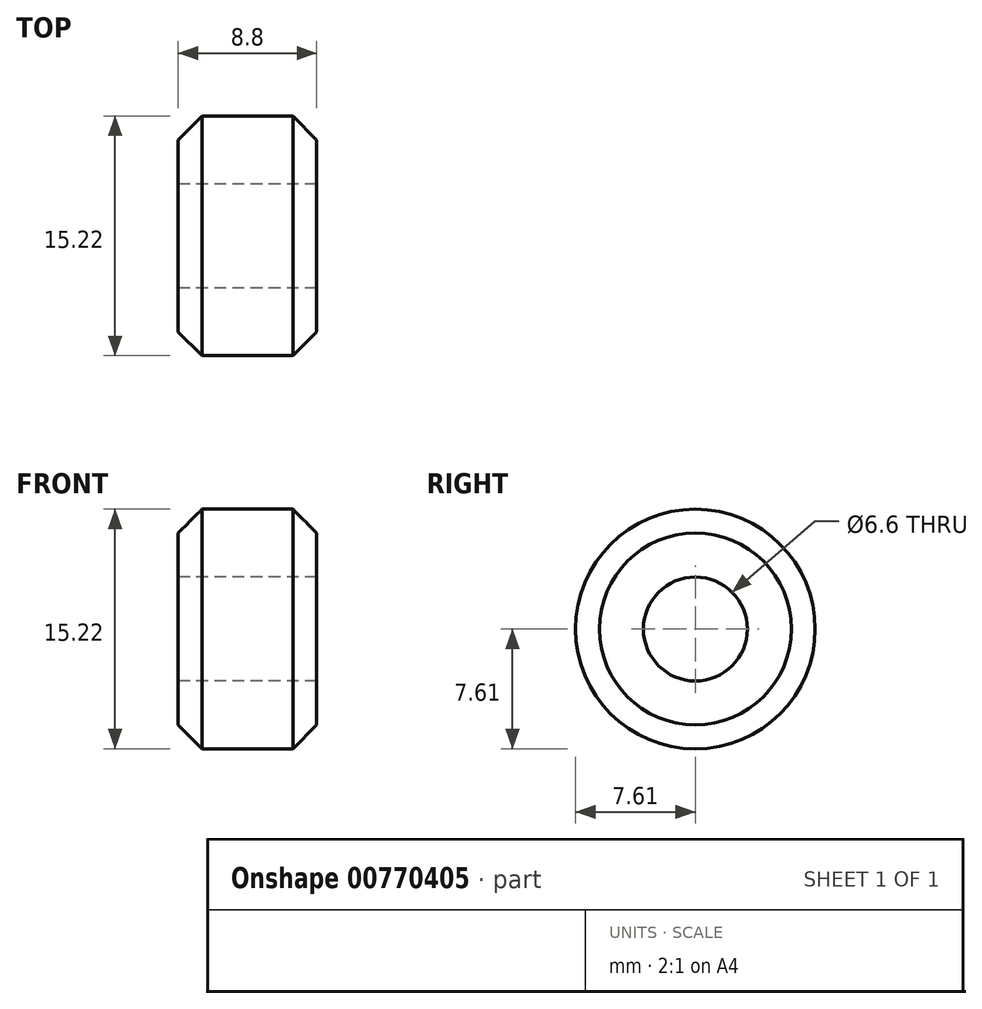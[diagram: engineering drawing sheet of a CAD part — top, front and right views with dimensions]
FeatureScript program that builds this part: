
annotation { "Feature Type Name" : "Feature", "Feature Type Description" : "" }
export const myFeature = defineFeature(function(context is Context, id is Id, definition is map)
    precondition{}
    {
        {
            var Q0;
            Q0=qCreatedBy(makeId("Top.planeOp"),FACE);
            var sketch = newSketch(context, id + "F0", { "sketchPlane" : qUnion([Q0])});
            skLineSegment(sketch, "E0.bottom", {"start": v(0, 0) * mm, "end": v(4.4, 0) * mm, "construction": true});
            skLineSegment(sketch, "E0.left", {"start": v(0, 0) * mm, "end": v(0, 4.32) * mm, "construction": true});
            skLineSegment(sketch, "E1.top", {"start": v(0, 5) * mm, "end": v(0.5, 5) * mm});
            skLineSegment(sketch, "E1.left", {"start": v(0, 4.32) * mm, "end": v(0, 5) * mm, "construction": true});
            skLineSegment(sketch, "E1.right", {"start": v(0.5, 4.32) * mm, "end": v(0.5, 5) * mm});
            skLineSegment(sketch, "E2.bottom", {"start": v(0, 5) * mm, "end": v(4.4, 5) * mm});
            skLineSegment(sketch, "E2.top", {"start": v(0, 7.6) * mm, "end": v(2.89, 7.61) * mm});
            skLineSegment(sketch, "E2.left", {"start": v(0, 5) * mm, "end": v(0, 7.61) * mm, "construction": true});
            skLineSegment(sketch, "E2.right", {"start": v(4.4, 5) * mm, "end": v(4.4, 6.1) * mm});
            skLineSegment(sketch, "E3", {"start": v(4.4, 6.1) * mm, "end": v(2.89, 7.61) * mm});
            skPoint(sketch, "E4.orphan", {"position": v(4.4, 7.61) * mm});
            skLineSegment(sketch, "E5", {"start": v(0, 4.32) * mm, "end": v(0.5, 4.32) * mm});
            skLineSegment(sketch, "E6.MirrorCS", {"start": v(0, 7.6) * mm, "end": v(-2.89, 7.61) * mm});
            skLineSegment(sketch, "E7.MirrorCS", {"start": v(-4.4, 6.1) * mm, "end": v(-2.89, 7.61) * mm});
            skLineSegment(sketch, "E8.MirrorCS", {"start": v(-4.4, 5) * mm, "end": v(-4.4, 6.1) * mm});
            skLineSegment(sketch, "E9.MirrorCS", {"start": v(0, 5) * mm, "end": v(-4.4, 5) * mm});
            skLineSegment(sketch, "E10.MirrorCS", {"start": v(-0.5, 4.32) * mm, "end": v(-0.5, 5) * mm});
            skLineSegment(sketch, "E11.MirrorCS", {"start": v(0, 4.32) * mm, "end": v(-0.5, 4.32) * mm});
            skSolve(sketch);
        }
        {
            var Q0;
            Q0=makeQuery(id+"F0.imprint","IMPRINT",FACE,{"disambiguationData":[TD([[makeQuery(id+"F0.imprint","IMPRINT",EDGE,{"derivedFrom":sQuery(id+"F0.wireOp",EDGE,"E2.top")}),-1.0]])]});
            var Q1;
            {var subQ4=sQuery(id+"F0.wireOp",EDGE,"E1.right");Q1=makeQuery(id+"F0.imprint","IMPRINT",FACE,{"disambiguationData":[TD([[makeQuery(id+"F0.imprint","IMPRINT",EDGE,{"derivedFrom":subQ4}),1.0]])]});}
            var Q2;
            Q2=sQuery(id+"F0.wireOp",EDGE,"E0.bottom");
            revolve(context, id + "F5", {"entities" : qUnion([Q0, Q1]), "axis" : qUnion([Q2]), "revolveType" : RevolveType.FULL});
        }
        {
            var Q0;
            Q0=makeQuery(id+"F5.opRevolve","SWEPT_FACE",FACE,{"disambiguationData":[OSD([sQuery(id+"F0.wireOp",EDGE,"E10.MirrorCS")])]});
            var Q1;
            Q1=makeQuery(id+"F5.opRevolve","SWEPT_FACE",FACE,{"disambiguationData":[OSD([sQuery(id+"F0.wireOp",EDGE,"E2.right")])]});
            var Q2;
            Q2=makeQuery(id+"F5.opRevolve","SWEPT_FACE",FACE,{"disambiguationData":[OSD([sQuery(id+"F0.wireOp",EDGE,"E8.MirrorCS")])]});
            extrude(context, id + "F1", {"entities" : qUnion([Q0]), "operationType" : NewBodyOperationType.ADD, "endBound" : BoundingType.UP_TO_SURFACE, "oppositeDirection" : true, "depth" : 25 * mm, "endBoundEntityFace" : qUnion([Q1]), "offsetDistance" : 25 * mm, "hasSecondDirection" : true, "secondDirectionBound" : SecondDirectionBoundingType.UP_TO_SURFACE, "secondDirectionOppositeDirection" : false, "secondDirectionDepth" : 25 * mm, "secondDirectionBoundEntityFace" : qUnion([Q2])});
        }
        {
            var Q0;
            {var subQ0=sQuery(id+"F0.wireOp",EDGE,"E8.MirrorCS");Q0=makeQuery(id+"F1.boolean.opBoolean","MERGE",FACE,{"derivedFrom":[makeQuery(id+"F5.opRevolve","SWEPT_FACE",FACE,{"disambiguationData":[OSD([subQ0])]}),makeQuery(id+"F1.opExtrude","CAP_FACE",FACE,{"disambiguationData":[OSD([subQ0])],"isStart":true})]});}
            var sketch = newSketch(context, id + "F2", { "sketchPlane" : qUnion([Q0])});
            skCircle(sketch, "E12.0", {"center": v(0, 0) * mm, "radius": 4.32 * mm});
            skSolve(sketch);
        }
        {
            var Q0;
            Q0 = qSketchRegion(id + "F2", true);
            var Q1;
            {var subQ0=sQuery(id+"F0.wireOp",EDGE,"E2.right");Q1=makeQuery(id+"F1.boolean.opBoolean","MERGE",FACE,{"derivedFrom":[makeQuery(id+"F5.opRevolve","SWEPT_FACE",FACE,{"disambiguationData":[OSD([subQ0])]}),makeQuery(id+"F1.opExtrude","CAP_FACE",FACE,{"disambiguationData":[OSD([subQ0])],"isStart":false})]});}
            extrude(context, id + "F3", {"entities" : qUnion([Q0]), "operationType" : NewBodyOperationType.ADD, "endBound" : BoundingType.UP_TO_SURFACE, "oppositeDirection" : true, "depth" : 25 * mm, "endBoundEntityFace" : qUnion([Q1]), "offsetDistance" : 25 * mm});
        }
        {
            var Q0;
            Q0=sQuery(id+"F2.wireOp",VERTEX,"E12.0.center");
            var Q1;
            Q1=makeQuery(id+"F5.opRevolve","SWEPT_BODY",BODY,{"disambiguationData":[OSD([sQuery(id+"F0.wireOp",EDGE,"E1.right"),sQuery(id+"F0.wireOp",EDGE,"E2.bottom"),sQuery(id+"F0.wireOp",EDGE,"E2.top"),sQuery(id+"F0.wireOp",EDGE,"E2.right"),sQuery(id+"F0.wireOp",EDGE,"E3"),sQuery(id+"F0.wireOp",EDGE,"E5"),sQuery(id+"F0.wireOp",EDGE,"E6.MirrorCS"),sQuery(id+"F0.wireOp",EDGE,"E7.MirrorCS"),sQuery(id+"F0.wireOp",EDGE,"E8.MirrorCS"),sQuery(id+"F0.wireOp",EDGE,"E9.MirrorCS"),sQuery(id+"F0.wireOp",EDGE,"E10.MirrorCS"),sQuery(id+"F0.wireOp",EDGE,"E11.MirrorCS")])]});
            hole(context, id + "F4", {"style" : HoleStyle.SIMPLE, "endStyle" : HoleEndStyle.THROUGH, "standardTappedOrClearance" : lookupTablePath({ "standard" : "ISO", "fit" : "Normal", "size" : "M6", "type" : "Clearance" }), "standardBlindInLast" : lookupTablePath({ "fit" : "Standard", "standard" : "ISO", "size" : "M6", "type" : "Clearance" }), "holeDiameter" : 6.6 * mm, "majorDiameter" : 5 * mm, "isTappedThrough" : true, "tappedDepth" : 12 * mm, "tapClearance" : 3, "locations" : qUnion([Q0]), "scope" : qUnion([Q1])});
        }
    });
